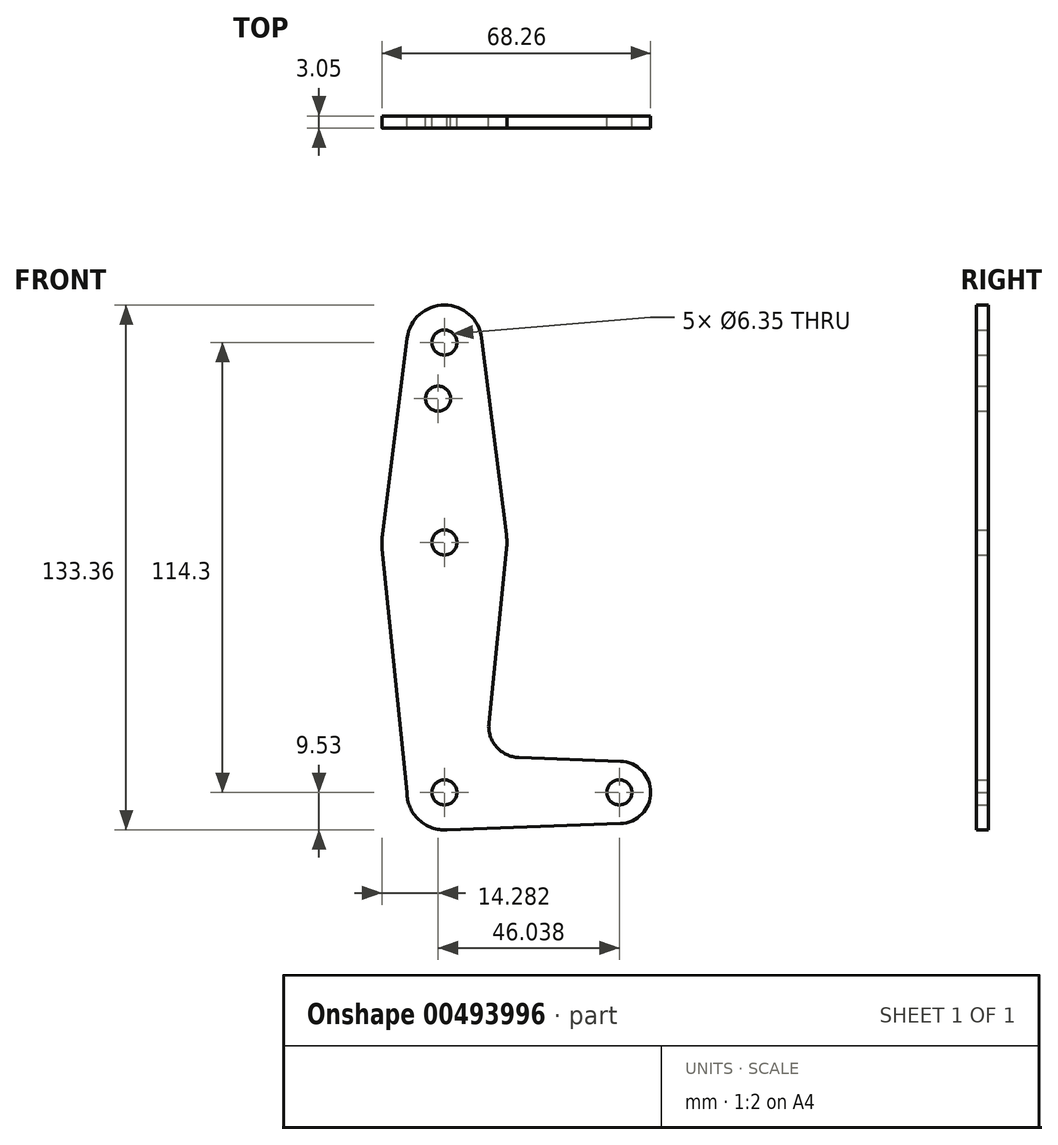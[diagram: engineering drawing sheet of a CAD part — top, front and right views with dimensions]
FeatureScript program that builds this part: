
annotation { "Feature Type Name" : "Feature", "Feature Type Description" : "" }
export const myFeature = defineFeature(function(context is Context, id is Id, definition is map)
    precondition{}
    {
        {
            var Q0;
            Q0=qCreatedBy(makeId("Front.planeOp"),FACE);
            var sketch = newSketch(context, id + "F0", { "sketchPlane" : qUnion([Q0])});
            skLineSegment(sketch, "E0", {"start": v(0, 0) * mm, "end": v(0, 114.3) * mm, "construction": true});
            skLineSegment(sketch, "E1", {"start": v(0, 0) * mm, "end": v(44.45, 0) * mm, "construction": true});
            skCircle(sketch, "E2", {"center": v(0, 114.3) * mm, "radius": 9.53 * mm});
            skCircle(sketch, "E3", {"center": v(0, 63.5) * mm, "radius": 15.88 * mm});
            skCircle(sketch, "E4", {"center": v(0, 0) * mm, "radius": 9.53 * mm});
            skCircle(sketch, "E5", {"center": v(44.45, 0) * mm, "radius": 7.94 * mm});
            skLineSegment(sketch, "E6", {"start": v(-9.45, 115.5) * mm, "end": v(-15.75, 65.48) * mm});
            skLineSegment(sketch, "E7", {"start": v(9.45, 115.5) * mm, "end": v(15.75, 65.48) * mm});
            skLineSegment(sketch, "E8", {"start": v(18.93, 8.85) * mm, "end": v(44.73, 7.93) * mm});
            skLineSegment(sketch, "E9", {"start": v(0, -9.52) * mm, "end": v(44.73, -7.93) * mm});
            skLineSegment(sketch, "E10", {"start": v(-9.53, 0) * mm, "end": v(-15.8, 61.9) * mm});
            skLineSegment(sketch, "E11", {"start": v(11.3, 17.6) * mm, "end": v(15.8, 61.9) * mm});
            skCircle(sketch, "E12", {"center": v(0, 114.3) * mm, "radius": 3.18 * mm});
            skCircle(sketch, "E13", {"center": v(0, 63.5) * mm, "radius": 3.18 * mm});
            skCircle(sketch, "E14", {"center": v(0, 0) * mm, "radius": 3.18 * mm});
            skCircle(sketch, "E15", {"center": v(44.45, 0) * mm, "radius": 3.18 * mm});
            skCircle(sketch, "E16", {"center": v(-1.59, 100.03) * mm, "radius": 3.18 * mm});
            skArc(sketch, "E17.filletArc", {"start": v(11.3, 17.6) * mm, "mid": v(13.22, 11.57) * mm, "end": v(18.93, 8.85) * mm});
            skSolve(sketch);
        }
        {
            var Q0;
            Q0 = qSketchRegion(id + "F0", true);
            extrude(context, id + "F1", {"entities" : qUnion([Q0]), "depth" : 3.05 * mm});
        }
    });
